# Revit family: Air Terminals_IVA
name_source: partatom
category: Air Terminals
revit_build: Autodesk Revit 2017 (Build: 20160225_1515(x64)
units: mm (PartAtom-declared; Revit-internal decimal feet)

## family parameters
Always vertical = Yes
Cut with Voids When Loaded = No
Part Type = Normal
Room Calculation Point = No
Round Connector Dimension = Use Diameter
Shared = No
Work Plane-Based = No

## types (8) — shared parameters
Lwa (dB(A)) = 35/45/55
Masse (kg) = 0
Max Flow = 0.0 L/s
Min Flow = 0.0 L/s

## per-type parameters (varying)
| type | Array radial | DN | H_Assembly | Maß A | Maß ØD | Vo (m3/h) | Void 7 | Void 8 | hori. Wurfw. xhor (m) | vert. Eindringt. ymax (m) | ∆p (Pa) |
| IVA_DN 250 | 14 | 1 | 540 mm  [stored 1.77165 ft] | 785.5 mm  [stored 2.5771 ft] | 248 mm  [stored 0.813648 ft] | 620/930/1350 | No | No | 0.8/0.9/1.1 | 3.5/4.9/6.6 | 12/27/56 |
| IVA_DN 315 | 15 | 2 | 540 mm  [stored 1.77165 ft] | 785.5 mm  [stored 2.5771 ft] | 313 mm  [stored 1.0269 ft] | 1050/1550/2150 | No | No | 1.3/1.6/1.8 | 4.7/6.5/8.6 | 14/30/58 |
| IVA_DN 355 | 16 | 3 | 540 mm  [stored 1.77165 ft] | 843.5 mm  [stored 2.76739 ft] | 353 mm  [stored 1.15814 ft] | 1350/2000/2800 | No | No | 1.7/2.0/2.3 | 5.5/7.5/9.9 | 14/31/61 |
| IVA_DN 400 | 17 | 4 | 540 mm  [stored 1.77165 ft] | 843.5 mm  [stored 2.76739 ft] | 398 mm  [stored 1.30577 ft] | 1700/2500/3500 | No | No | 2.3/2.6/3.0 | 6.3/8.6/11.4 | 15/32/62 |
| IVA_DN 450 | 18 | 5 | 540 mm  [stored 1.77165 ft] | 843.5 mm  [stored 2.76739 ft] | 448 mm  [stored 1.46982 ft] | 2100/3100/4400 | No | No | 2.9/3.4/3.9 | 7.0/9.7/13.0 | 14/31/63 |
| IVA_DN 500 | 20 | 6 | 660 mm | 951.5 mm  [stored 3.12172 ft] | 498 mm  [stored 1.63386 ft] | 2650/4000/5600 | Yes | No | 3.6/4.3/4.9 | 7.9/11.0/14.6 | 14/32/63 |
| IVA_DN 560 | 22 | 7 | 780 mm  [stored 2.55906 ft] | 1059.5 mm | 558 mm | 3300/5000/7100 | Yes | Yes | 4.6/5.4/6.2 | 8.8/12.3/16.5 | 13/31/63 |
| IVA_DN 630 | 24 | 8 | 780 mm  [stored 2.55906 ft] | 1059.5 mm | 628 mm  [stored 2.06037 ft] | 4100/6400/9200 | Yes | Yes | 5.8/6.9/8.0 | 9.7/14.0/18.9 | 13/31/65 |

note: [stored X ft] marks values corroborated as IEEE doubles in the binary element streams (Revit-internal decimal feet)

## geometry (parser evidence)
native form markers: Sweep x35
no freeform markers — native parametric forms only
